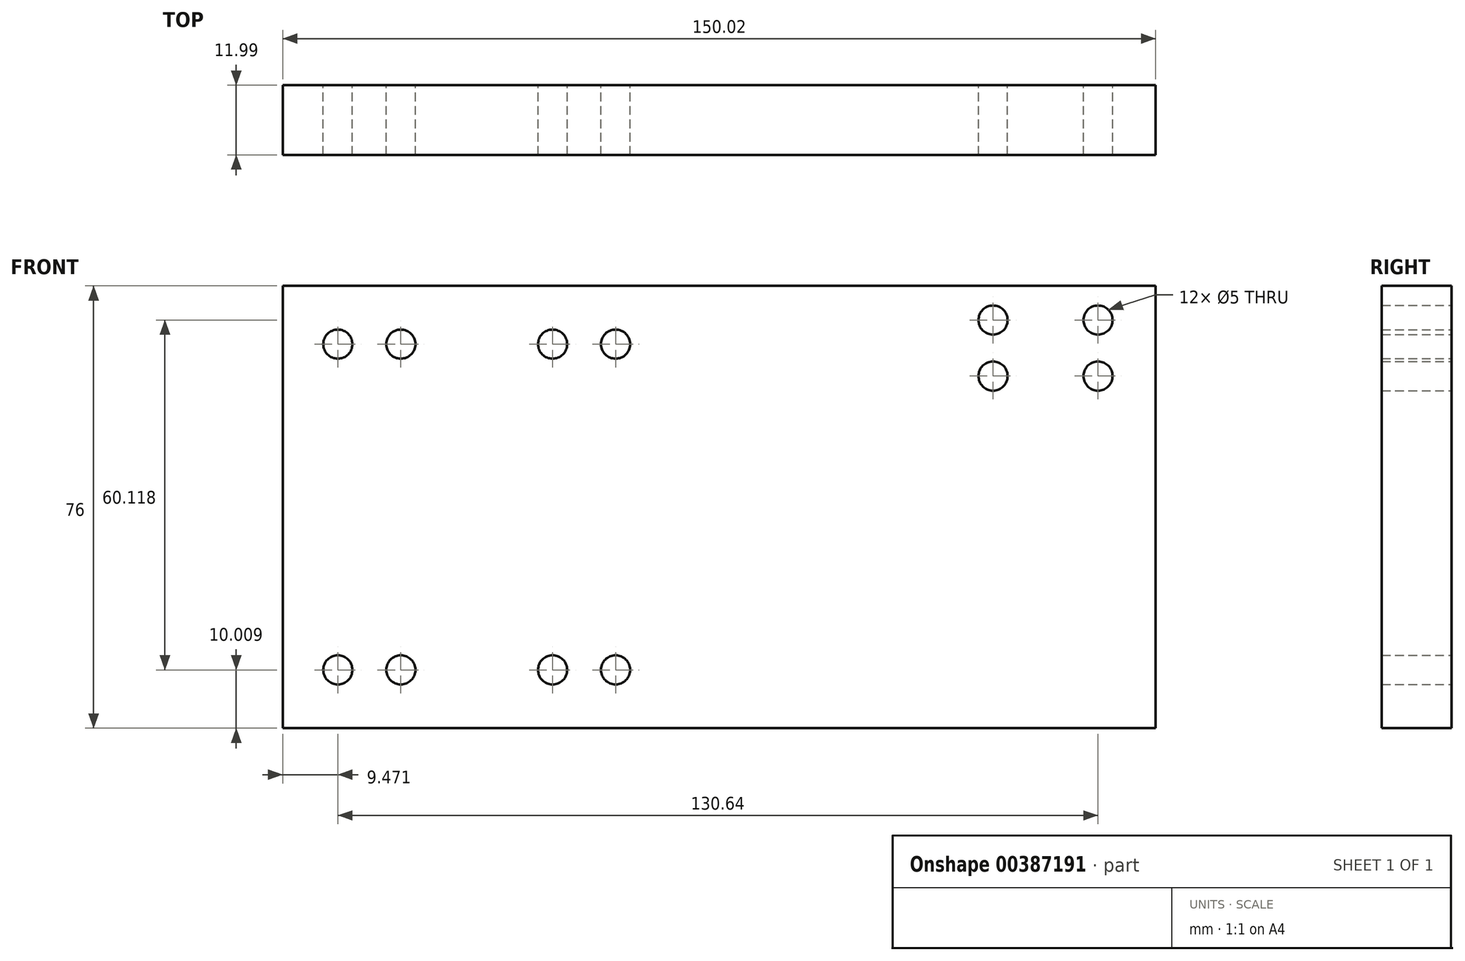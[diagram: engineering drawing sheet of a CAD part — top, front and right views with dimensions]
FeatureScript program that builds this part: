
annotation { "Feature Type Name" : "Feature", "Feature Type Description" : "" }
export const myFeature = defineFeature(function(context is Context, id is Id, definition is map)
    precondition{}
    {
        {
            var Q0;
            Q0=qCreatedBy(makeId("Front.planeOp"),FACE);
            var sketch = newSketch(context, id + "F0", { "sketchPlane" : qUnion([Q0])});
            skLineSegment(sketch, "E0.bottom", {"start": v(75, -38) * mm, "end": v(-75, -38) * mm});
            skLineSegment(sketch, "E0.top", {"start": v(75, 38) * mm, "end": v(-75, 38) * mm});
            skLineSegment(sketch, "E0.left", {"start": v(75, -38) * mm, "end": v(75, 38) * mm});
            skLineSegment(sketch, "E0.right", {"start": v(-75, -38) * mm, "end": v(-75, 38) * mm});
            skPoint(sketch, "E0.middle", {"position": v(0, 0) * mm});
            skCircle(sketch, "E1", {"center": v(-65.54, 28) * mm, "radius": 2.5 * mm});
            skCircle(sketch, "E2", {"center": v(-54.71, 28) * mm, "radius": 2.5 * mm});
            skCircle(sketch, "E3", {"center": v(-28.63, 28) * mm, "radius": 2.5 * mm});
            skCircle(sketch, "E4", {"center": v(-17.8, 28) * mm, "radius": 2.5 * mm});
            skCircle(sketch, "E5.MirrorC", {"center": v(-65.54, -28) * mm, "radius": 2.5 * mm});
            skCircle(sketch, "E6.MirrorC", {"center": v(-54.71, -28) * mm, "radius": 2.5 * mm});
            skCircle(sketch, "E7.MirrorC", {"center": v(-28.63, -28) * mm, "radius": 2.5 * mm});
            skCircle(sketch, "E8.MirrorC", {"center": v(-17.8, -28) * mm, "radius": 2.5 * mm});
            skCircle(sketch, "E9", {"center": v(65.1, 22.5) * mm, "radius": 2.5 * mm});
            skCircle(sketch, "E10", {"center": v(47.06, 22.5) * mm, "radius": 2.5 * mm});
            skCircle(sketch, "E11", {"center": v(65.1, 32.13) * mm, "radius": 2.5 * mm});
            skCircle(sketch, "E12", {"center": v(47.06, 32.13) * mm, "radius": 2.5 * mm});
            skSolve(sketch);
        }
        {
            var Q0;
            Q0=makeQuery(id+"F0.imprint","IMPRINT",FACE,{"disambiguationData":[TD([[makeQuery(id+"F0.imprint","IMPRINT",EDGE,{"derivedFrom":sQuery(id+"F0.wireOp",EDGE,"E0.bottom")}),-1.0]])]});
            extrude(context, id + "F1", {"entities" : qUnion([Q0]), "depth" : 12 * mm});
        }
    });
